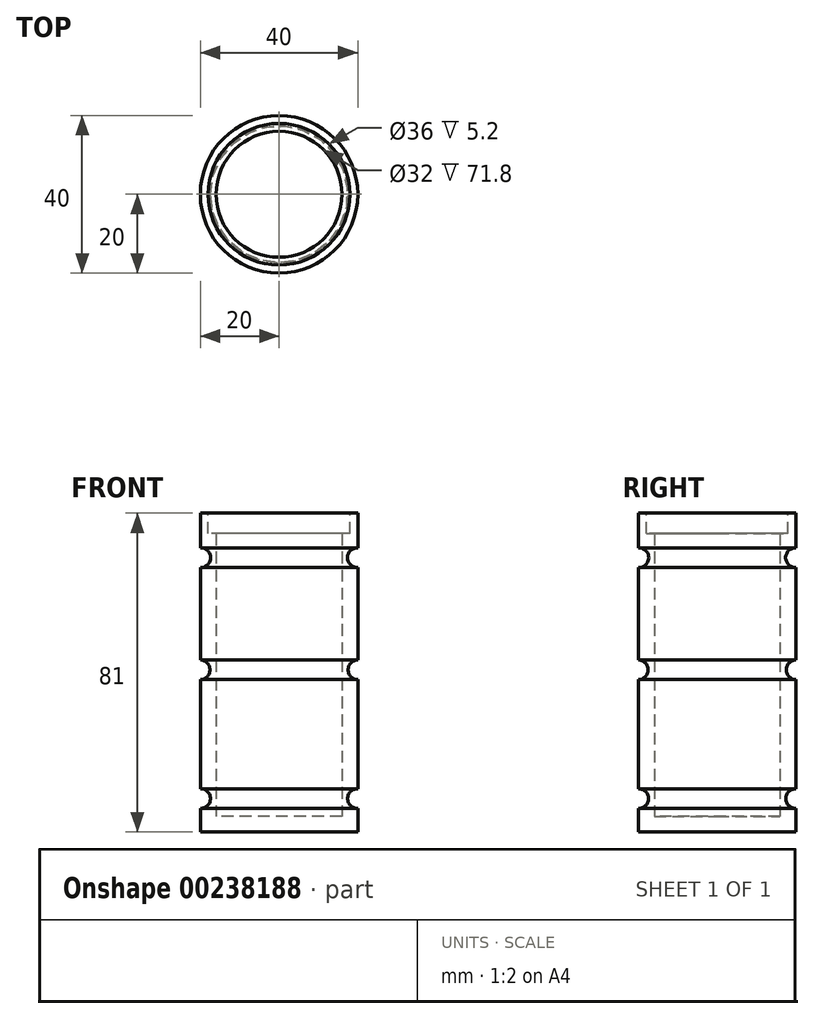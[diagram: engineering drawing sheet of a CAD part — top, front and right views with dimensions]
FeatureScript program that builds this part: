
annotation { "Feature Type Name" : "Feature", "Feature Type Description" : "" }
export const myFeature = defineFeature(function(context is Context, id is Id, definition is map)
    precondition{}
    {
        {
            var Q0;
            Q0=qCreatedBy(makeId("Top.planeOp"),FACE);
            var sketch = newSketch(context, id + "F0", { "sketchPlane" : qUnion([Q0])});
            skCircle(sketch, "E0", {"center": v(0, 0) * mm, "radius": 20 * mm});
            skSolve(sketch);
        }
        {
            var Q0;
            Q0=makeQuery(id+"F0.imprint","IMPRINT",FACE,{"disambiguationData":[TD([[makeQuery(id+"F0.imprint","IMPRINT",EDGE,{"derivedFrom":sQuery(id+"F0.wireOp",EDGE,"E0")}),1.0]])]});
            extrude(context, id + "F1", {"entities" : qUnion([Q0]), "depth" : 81 * mm, "offsetDistance" : 25 * mm});
        }
        {
            var Q0;
            Q0=makeQuery(id+"F1.opExtrude","CAP_FACE",FACE,{"disambiguationData":[OSD([sQuery(id+"F0.wireOp",EDGE,"E0")])],"isStart":false});
            shell(context, id + "F2", {"entities" : qUnion([Q0]), "thickness" : 4 * mm});
        }
        {
            var Q0;
            Q0=makeQuery(id+"F1.opExtrude","CAP_FACE",FACE,{"disambiguationData":[OSD([sQuery(id+"F0.wireOp",EDGE,"E0")])],"isStart":false});
            var sketch = newSketch(context, id + "F3", { "sketchPlane" : qUnion([Q0])});
            skCircle(sketch, "E1", {"center": v(0, 0) * mm, "radius": 18 * mm});
            skSolve(sketch);
        }
        {
            var Q0;
            Q0 = qSketchRegion(id + "F3", true);
            extrude(context, id + "F4", {"entities" : qUnion([Q0]), "operationType" : NewBodyOperationType.REMOVE, "oppositeDirection" : true, "depth" : 5.2 * mm, "offsetDistance" : 25 * mm});
        }
        {
            var Q0;
            Q0=qCreatedBy(makeId("Front.planeOp"),FACE);
            var sketch = newSketch(context, id + "F5", { "sketchPlane" : qUnion([Q0])});
            skCircle(sketch, "E2", {"center": v(-19.88, 69.69) * mm, "radius": 2.5 * mm});
            skCircle(sketch, "E3", {"center": v(-19.93, 8.47) * mm, "radius": 2.5 * mm});
            skCircle(sketch, "E4", {"center": v(-20.05, 41.2) * mm, "radius": 2.5 * mm});
            skSolve(sketch);
        }
        {
            var Q0;
            Q0=qCreatedBy(makeId("Front.planeOp"),FACE);
            var sketch = newSketch(context, id + "F6", { "sketchPlane" : qUnion([Q0])});
            skLineSegment(sketch, "E5", {"start": v(0, 74.73) * mm, "end": v(0, 0) * mm});
            skSolve(sketch);
        }
        {
            var Q0;
            Q0 = qSketchRegion(id + "F6", true);
            var Q1;
            Q1=makeQuery(id+"F5.imprint","IMPRINT",FACE,{"disambiguationData":[TD([[makeQuery(id+"F5.imprint","IMPRINT",EDGE,{"derivedFrom":sQuery(id+"F5.wireOp",EDGE,"E2")}),1.0]])]});
            var Q2;
            Q2=makeQuery(id+"F5.imprint","IMPRINT",FACE,{"disambiguationData":[TD([[makeQuery(id+"F5.imprint","IMPRINT",EDGE,{"derivedFrom":sQuery(id+"F5.wireOp",EDGE,"E3")}),1.0]])]});
            var Q3;
            Q3=makeQuery(id+"F5.imprint","IMPRINT",FACE,{"disambiguationData":[TD([[makeQuery(id+"F5.imprint","IMPRINT",EDGE,{"derivedFrom":sQuery(id+"F5.wireOp",EDGE,"E4")}),1.0]])]});
            var Q4;
            Q4=sQuery(id+"F6.wireOp",EDGE,"E5");
            revolve(context, id + "F7", {"operationType" : NewBodyOperationType.REMOVE, "entities" : qUnion([Q0, Q1, Q2, Q3]), "axis" : qUnion([Q4]), "revolveType" : RevolveType.FULL, "oppositeDirection" : true});
        }
    });
